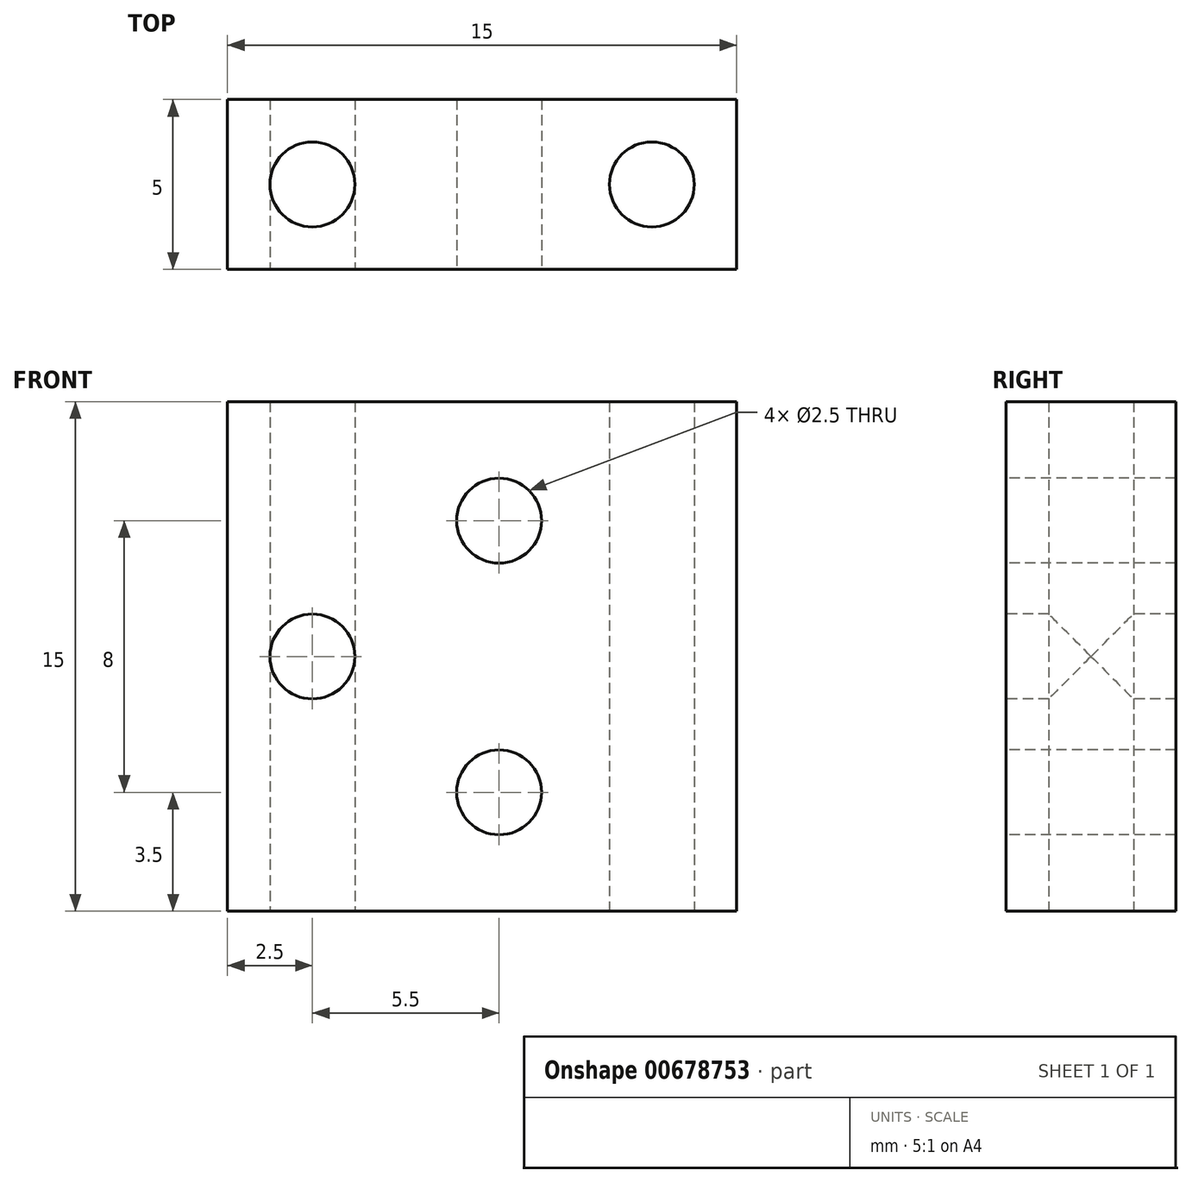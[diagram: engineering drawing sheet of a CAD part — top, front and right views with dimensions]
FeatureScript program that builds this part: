
annotation { "Feature Type Name" : "Feature", "Feature Type Description" : "" }
export const myFeature = defineFeature(function(context is Context, id is Id, definition is map)
    precondition{}
    {
        {
            var Q0;
            Q0=qCreatedBy(makeId("Top.planeOp"),FACE);
            var sketch = newSketch(context, id + "F0", { "sketchPlane" : qUnion([Q0])});
            skCircle(sketch, "E0", {"center": v(-5, 0) * mm, "radius": 1.25 * mm});
            skCircle(sketch, "E1", {"center": v(5, 0) * mm, "radius": 1.25 * mm});
            skLineSegment(sketch, "E2.bottom", {"start": v(-7.5, -2.5) * mm, "end": v(7.5, -2.5) * mm});
            skLineSegment(sketch, "E2.top", {"start": v(-7.5, 2.5) * mm, "end": v(7.5, 2.5) * mm});
            skLineSegment(sketch, "E2.left", {"start": v(-7.5, -2.5) * mm, "end": v(-7.5, 2.5) * mm});
            skLineSegment(sketch, "E2.right", {"start": v(7.5, -2.5) * mm, "end": v(7.5, 2.5) * mm});
            skPoint(sketch, "E2.middle", {"position": v(0, 0) * mm});
            skSolve(sketch);
        }
        {
            var Q0;
            Q0=makeQuery(id+"F0.imprint","IMPRINT",FACE,{"disambiguationData":[TD([[makeQuery(id+"F0.imprint","IMPRINT",EDGE,{"derivedFrom":sQuery(id+"F0.wireOp",EDGE,"E0")}),-1.0]])]});
            extrude(context, id + "F1", {"entities" : qUnion([Q0]), "depth" : 15 * mm, "offsetDistance" : 25 * mm});
        }
        {
            var Q0;
            Q0=makeQuery(id+"F1.opExtrude","SWEPT_FACE",FACE,{"disambiguationData":[OSD([sQuery(id+"F0.wireOp",EDGE,"E2.bottom")])]});
            var sketch = newSketch(context, id + "F2", { "sketchPlane" : qUnion([Q0])});
            skPoint(sketch, "E3", {"position": v(0.5, 11.5) * mm});
            skPoint(sketch, "E4", {"position": v(0.5, 3.5) * mm});
            skPoint(sketch, "E5", {"position": v(-5, 7.5) * mm});
            skSolve(sketch);
        }
        {
            var Q0;
            Q0=sQuery(id+"F2.wireOp",VERTEX,"E3");
            var Q1;
            Q1=sQuery(id+"F2.wireOp",VERTEX,"E5");
            var Q2;
            Q2=sQuery(id+"F2.wireOp",VERTEX,"E4");
            var Q3;
            Q3=makeQuery(id+"F1.opExtrude","SWEPT_BODY",BODY,{"disambiguationData":[OSD([sQuery(id+"F0.wireOp",EDGE,"E0"),sQuery(id+"F0.wireOp",EDGE,"E1"),sQuery(id+"F0.wireOp",EDGE,"E2.bottom"),sQuery(id+"F0.wireOp",EDGE,"E2.top"),sQuery(id+"F0.wireOp",EDGE,"E2.left"),sQuery(id+"F0.wireOp",EDGE,"E2.right")])]});
            hole(context, id + "F3", {"style" : HoleStyle.SIMPLE, "endStyle" : HoleEndStyle.THROUGH, "standardTappedOrClearance" : lookupTablePath({ "standard" : "ISO", "engagement" : "75%", "pitch" : "0.5 mm", "size" : "M3", "type" : "Tapped" }), "standardBlindInLast" : lookupTablePath({ "standard" : "ISO", "engagement" : "75%", "pitch" : "0.5 mm", "size" : "M3", "type" : "Tapped" }), "holeDiameter" : 2.5 * mm, "majorDiameter" : 3 * mm, "showTappedDepth" : true, "isTappedThrough" : true, "tappedDepth" : 6 * mm, "tapClearance" : 3, "locations" : qUnion([Q0, Q1, Q2]), "scope" : qUnion([Q3])});
        }
    });
